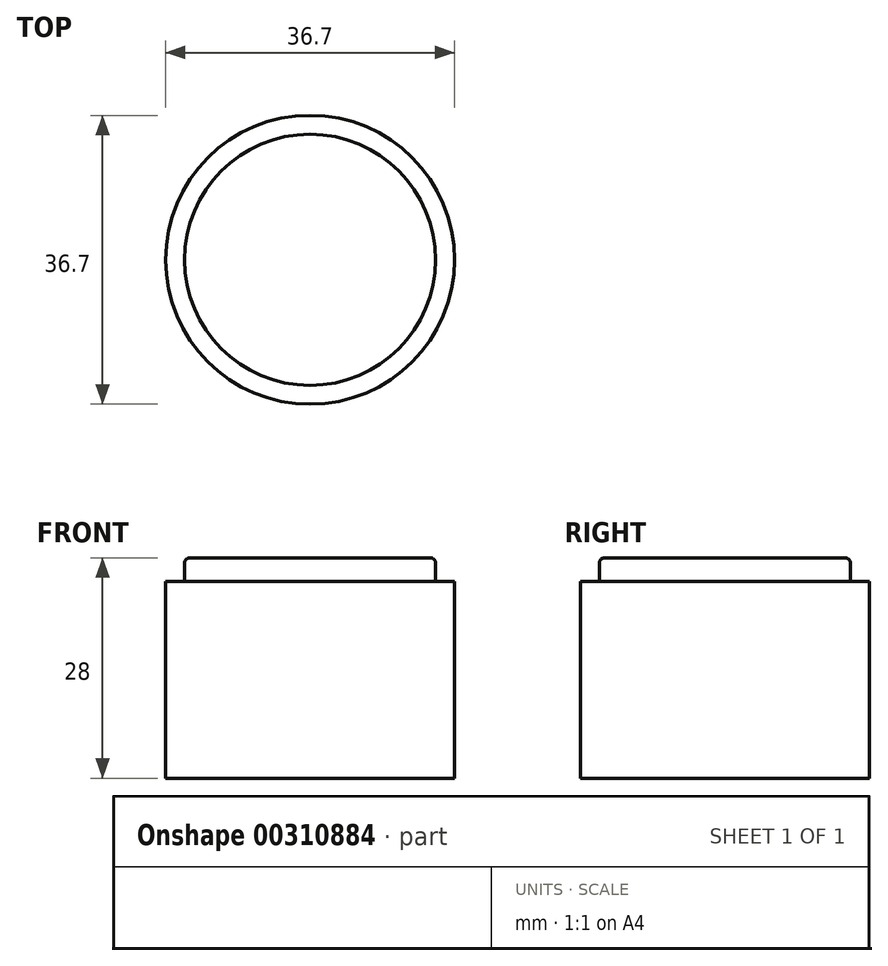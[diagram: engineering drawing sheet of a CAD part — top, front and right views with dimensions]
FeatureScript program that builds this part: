
annotation { "Feature Type Name" : "Feature", "Feature Type Description" : "" }
export const myFeature = defineFeature(function(context is Context, id is Id, definition is map)
    precondition{}
    {
        {
            var Q0;
            Q0=qCreatedBy(makeId("Top.planeOp"),FACE);
            var sketch = newSketch(context, id + "F0", { "sketchPlane" : qUnion([Q0])});
            skCircle(sketch, "E0", {"center": v(0, 0) * mm, "radius": 18.35 * mm});
            skSolve(sketch);
        }
        {
            var Q0;
            Q0=makeQuery(id+"F0.imprint","IMPRINT",FACE,{"disambiguationData":[TD([[makeQuery(id+"F0.imprint","IMPRINT",EDGE,{"derivedFrom":sQuery(id+"F0.wireOp",EDGE,"E0")}),1.0]])]});
            var Q1;
            Q1=sQuery(id+"F0.wireOp",EDGE,"E0");
            extrude(context, id + "F1", {"entities" : qUnion([Q0]), "surfaceEntities" : qUnion([Q1]), "depth" : 25 * mm});
        }
        {
            var Q0;
            Q0=makeQuery(id+"F1.opExtrude","CAP_FACE",FACE,{"disambiguationData":[OSD([sQuery(id+"F0.wireOp",EDGE,"E0")])],"isStart":false});
            var sketch = newSketch(context, id + "F2", { "sketchPlane" : qUnion([Q0])});
            skCircle(sketch, "E1", {"center": v(0, 0) * mm, "radius": 15.95 * mm});
            skSolve(sketch);
        }
        {
            var Q0;
            Q0=qSketchRegion(id+"F2",true);
            extrude(context, id + "F3", {"entities" : qUnion([Q0]), "operationType" : NewBodyOperationType.ADD, "depth" : 3 * mm});
        }
        {
            var Q0;
            Q0=makeQuery(id+"F3.opExtrude","CAP_EDGE",EDGE,{"disambiguationData":[OSD([sQuery(id+"F2.wireOp",EDGE,"E1")])],"isStart":false});
            fillet(context, id + "F4", {"entities" : qUnion([Q0]), "radius" : .7 * mm, "tangentPropagation" : true, "allowEdgeOverflow" : false});
        }
    });
